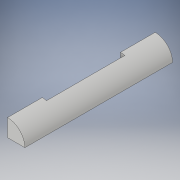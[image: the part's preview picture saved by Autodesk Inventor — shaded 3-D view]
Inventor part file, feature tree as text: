
AUTODESK INVENTOR PART (.ipt)
format: ipt  version: 2019.1 (Build 231200000, 200)  size: 109,056 bytes
history: native  units: in
note: dims shown in document units (in); Inventor stores cm internally (conversion verified against a paired STEP export)
features: extrude x2, sketch x2
ambient origin geometry x8: Origin, YZ Plane, XZ Plane, XY Plane, X Axis, Y Axis, Z Axis, Center Point
bodies: Solid1 (feature_tree)
feature tree (4):
  extrude  "Extrusion1"  Depth=6.375in TaperAngle=0.0deg
  extrude  "Extrusion2"  Depth=1.5in
  sketch  "Sketch1"  dims[d0=1.5in d1=6.375in d2=0.0in]
  sketch  "Sketch2"  dims[d3=3.375in d4=1.5in d5=0.1875in d6=0.0in d7=0.0in]
